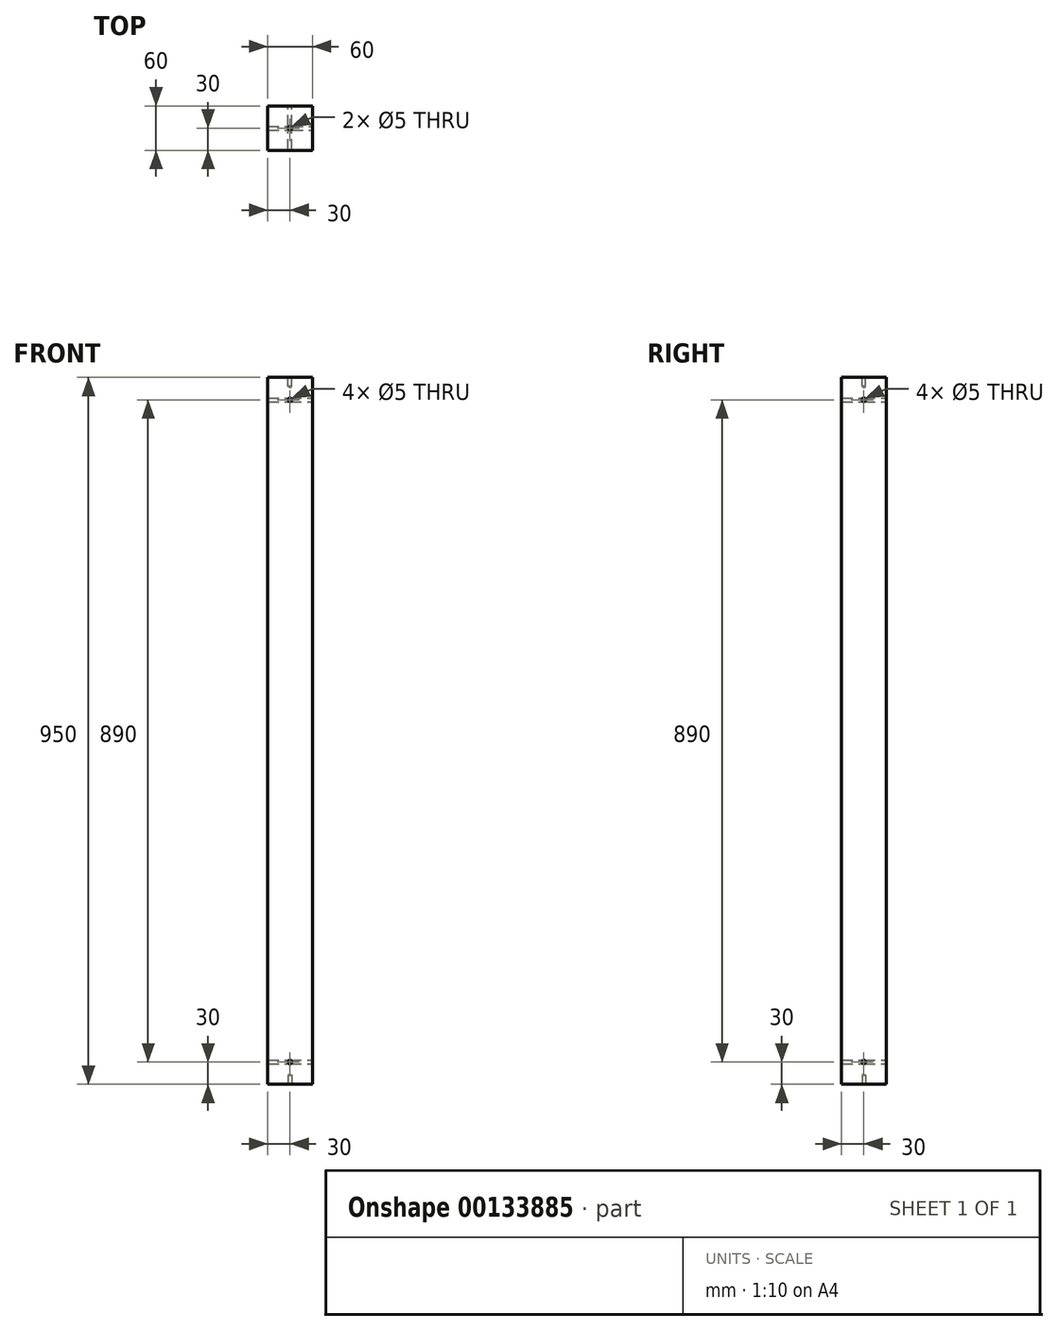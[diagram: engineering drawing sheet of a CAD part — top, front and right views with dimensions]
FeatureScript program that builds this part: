
annotation { "Feature Type Name" : "Feature", "Feature Type Description" : "" }
export const myFeature = defineFeature(function(context is Context, id is Id, definition is map)
    precondition{}
    {
        {
            assignVariable(context, id + "F0", {"name" : "Laenge", "anyValue" : 950 * mm});
        }
        {
            var Q0;
            Q0=qCreatedBy(makeId("Top.planeOp"),FACE);
            var sketch = newSketch(context, id + "F1", { "sketchPlane" : qUnion([Q0])});
            skLineSegment(sketch, "E0.bottom", {"start": v(-30, 30) * mm, "end": v(30, 30) * mm});
            skLineSegment(sketch, "E0.top", {"start": v(-30, -30) * mm, "end": v(30, -30) * mm});
            skLineSegment(sketch, "E0.left", {"start": v(-30, 30) * mm, "end": v(-30, -30) * mm});
            skLineSegment(sketch, "E0.right", {"start": v(30, 30) * mm, "end": v(30, -30) * mm});
            skPoint(sketch, "E1", {"position": v(0, 30) * mm});
            skPoint(sketch, "E2", {"position": v(30, 0) * mm});
            skLineSegment(sketch, "E3", {"start": v(0, 30) * mm, "end": v(0, 0) * mm, "construction": true});
            skLineSegment(sketch, "E4", {"start": v(0, 0) * mm, "end": v(30, 0) * mm, "construction": true});
            skSolve(sketch);
        }
        {
            var Q0;
            Q0 = qSketchRegion(id + "F1", true);
            extrude(context, id + "F2", {"entities" : qUnion([Q0]), "depth" : getVariable(context, 'Laenge')});
        }
        {
            var Q0;
            Q0=makeQuery(id+"F2.opExtrude","CAP_FACE",FACE,{"disambiguationData":[OSD([sQuery(id+"F1.wireOp",EDGE,"E0.bottom"),sQuery(id+"F1.wireOp",EDGE,"E0.top"),sQuery(id+"F1.wireOp",EDGE,"E0.left"),sQuery(id+"F1.wireOp",EDGE,"E0.right")])],"isStart":false});
            var sketch = newSketch(context, id + "F3", { "sketchPlane" : qUnion([Q0])});
            skPoint(sketch, "E5", {"position": v(0, 0) * mm});
            skSolve(sketch);
        }
        {
            var Q0;
            Q0=makeQuery(id+"F2.opExtrude","CAP_FACE",FACE,{"disambiguationData":[OSD([sQuery(id+"F1.wireOp",EDGE,"E0.bottom"),sQuery(id+"F1.wireOp",EDGE,"E0.top"),sQuery(id+"F1.wireOp",EDGE,"E0.left"),sQuery(id+"F1.wireOp",EDGE,"E0.right")])],"isStart":true});
            var sketch = newSketch(context, id + "F4", { "sketchPlane" : qUnion([Q0])});
            skPoint(sketch, "E6", {"position": v(0, 0) * mm});
            skSolve(sketch);
        }
        {
            var Q0;
            Q0=makeQuery(id+"F2.opExtrude","SWEPT_FACE",FACE,{"disambiguationData":[OSD([sQuery(id+"F1.wireOp",EDGE,"E0.right")])]});
            var sketch = newSketch(context, id + "F5", { "sketchPlane" : qUnion([Q0])});
            skPoint(sketch, "E7", {"position": v(0, 920) * mm});
            skLineSegment(sketch, "E8", {"start": v(30, 475) * mm, "end": v(-30, 475) * mm, "construction": true});
            skPoint(sketch, "E9.MirrorP", {"position": v(0, 30) * mm});
            skSolve(sketch);
        }
        {
            var Q0;
            Q0=makeQuery(id+"F2.opExtrude","SWEPT_FACE",FACE,{"disambiguationData":[OSD([sQuery(id+"F1.wireOp",EDGE,"E0.bottom")])]});
            var sketch = newSketch(context, id + "F6", { "sketchPlane" : qUnion([Q0])});
            skPoint(sketch, "E10", {"position": v(0, 920) * mm});
            skPoint(sketch, "E10.positionSnap0", {"position": v(0, 950) * mm});
            skLineSegment(sketch, "E11", {"start": v(30, 475) * mm, "end": v(-30, 475) * mm, "construction": true});
            skPoint(sketch, "E12.MirrorP", {"position": v(0, 30) * mm});
            skSolve(sketch);
        }
        {
            var Q0;
            Q0=sQuery(id+"F3.wireOp",VERTEX,"E5");
            var Q1;
            Q1=sQuery(id+"F4.wireOp",VERTEX,"E6");
            var Q2;
            Q2=makeQuery(id+"F2.opExtrude","SWEPT_BODY",BODY,{"disambiguationData":[OSD([sQuery(id+"F1.wireOp",EDGE,"E0.bottom"),sQuery(id+"F1.wireOp",EDGE,"E0.top"),sQuery(id+"F1.wireOp",EDGE,"E0.left"),sQuery(id+"F1.wireOp",EDGE,"E0.right")])]});
            hole(context, id + "F7", {"style" : HoleStyle.SIMPLE, "endStyle" : HoleEndStyle.BLIND, "holeDiameter" : 5 * mm, "holeDepth" : 12 * mm, "startFromSketch" : true, "locations" : qUnion([Q0, Q1]), "scope" : qUnion([Q2])});
        }
        {
            var Q0;
            Q0=sQuery(id+"F6.wireOp",VERTEX,"E10");
            var Q1;
            Q1=sQuery(id+"F5.wireOp",VERTEX,"E7");
            var Q2;
            Q2=sQuery(id+"F5.wireOp",VERTEX,"E9.MirrorP");
            var Q3;
            Q3=sQuery(id+"F6.wireOp",VERTEX,"E12.MirrorP");
            var Q4;
            Q4=makeQuery(id+"F2.opExtrude","SWEPT_BODY",BODY,{"disambiguationData":[OSD([sQuery(id+"F1.wireOp",EDGE,"E0.bottom"),sQuery(id+"F1.wireOp",EDGE,"E0.top"),sQuery(id+"F1.wireOp",EDGE,"E0.left"),sQuery(id+"F1.wireOp",EDGE,"E0.right")])]});
            hole(context, id + "F8", {"style" : HoleStyle.SIMPLE, "endStyle" : HoleEndStyle.THROUGH, "holeDiameter" : 5 * mm, "startFromSketch" : true, "locations" : qUnion([Q0, Q1, Q2, Q3]), "scope" : qUnion([Q4]), "isTappedThrough" : true});
        }
    });
